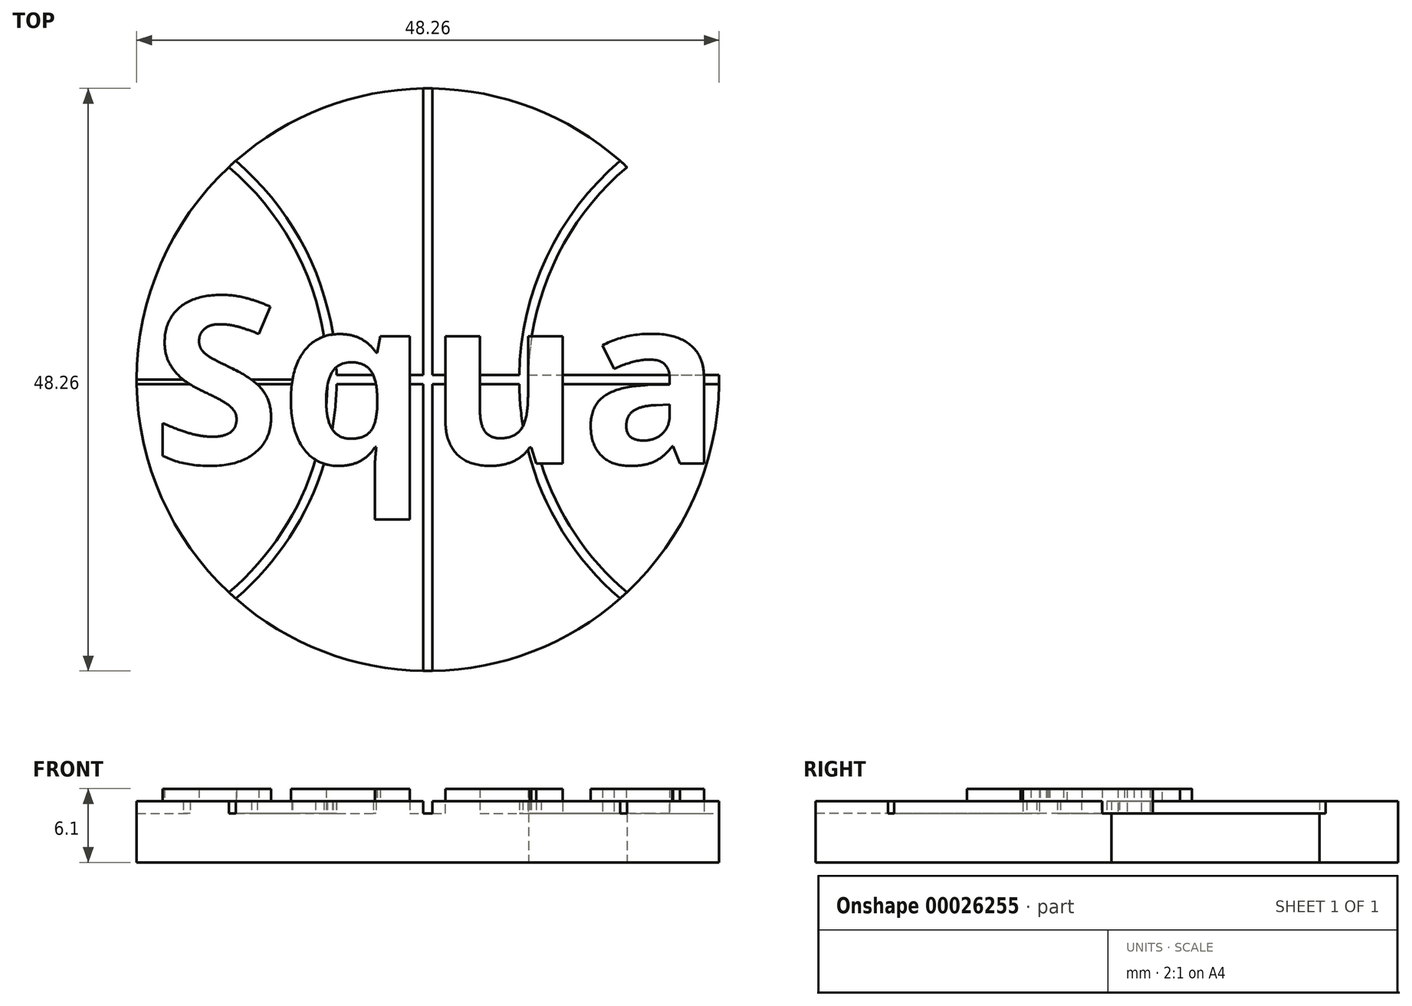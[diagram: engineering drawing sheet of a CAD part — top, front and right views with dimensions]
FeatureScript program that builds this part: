
annotation { "Feature Type Name" : "Feature", "Feature Type Description" : "" }
export const myFeature = defineFeature(function(context is Context, id is Id, definition is map)
    precondition{}
    {
        {
            var Q0;
            Q0=qCreatedBy(makeId("Top.planeOp"),FACE);
            var sketch = newSketch(context, id + "F0", { "sketchPlane" : qUnion([Q0])});
            skCircle(sketch, "E0", {"center": v(0, 0) * mm, "radius": 24.13 * mm});
            skLineSegment(sketch, "E1", {"start": v(-24.13, 0) * mm, "end": v(24.13, 0) * mm});
            skLineSegment(sketch, "E2", {"start": v(0, 24.13) * mm, "end": v(0, -24.13) * mm});
            skArc(sketch, "E3", {"start": v(-16.21, -17.87) * mm, "mid": v(-7.95, 0) * mm, "end": v(-16.21, 17.87) * mm});
            skArc(sketch, "E4.MirrorCS", {"start": v(16.21, -17.87) * mm, "mid": v(7.95, 0) * mm, "end": v(16.21, 17.87) * mm});
            skArc(sketch, "E5.0.startCap", {"start": v(-15.97, -18.16) * mm, "mid": v(-16.5, -18.12) * mm, "end": v(-16.46, -17.58) * mm});
            skArc(sketch, "E5.0.endCap", {"start": v(-16.46, 17.58) * mm, "mid": v(-16.5, 18.12) * mm, "end": v(-15.97, 18.16) * mm});
            skArc(sketch, "E5.0.left", {"start": v(-16.46, -17.58) * mm, "mid": v(-8.33, 0) * mm, "end": v(-16.46, 17.58) * mm});
            skArc(sketch, "E5.0.right", {"start": v(-15.97, -18.16) * mm, "mid": v(-7.56, 0) * mm, "end": v(-15.97, 18.16) * mm});
            skArc(sketch, "E6.0.startCap", {"start": v(-0.38, 24.13) * mm, "mid": v(0, 24.51) * mm, "end": v(0.38, 24.13) * mm});
            skArc(sketch, "E6.0.endCap", {"start": v(0.38, -24.13) * mm, "mid": v(0, -24.51) * mm, "end": v(-0.38, -24.13) * mm});
            skLineSegment(sketch, "E6.0.left", {"start": v(0.38, 24.13) * mm, "end": v(0.38, -24.13) * mm});
            skLineSegment(sketch, "E6.0.right", {"start": v(-0.38, 24.13) * mm, "end": v(-0.38, -24.13) * mm});
            skArc(sketch, "E6.1.startCap", {"start": v(-24.13, -0.38) * mm, "mid": v(-24.51, 0) * mm, "end": v(-24.13, 0.38) * mm});
            skArc(sketch, "E6.1.endCap", {"start": v(24.13, 0.38) * mm, "mid": v(24.51, 0) * mm, "end": v(24.13, -0.38) * mm});
            skLineSegment(sketch, "E6.1.left", {"start": v(-24.13, 0.38) * mm, "end": v(24.13, 0.38) * mm});
            skLineSegment(sketch, "E6.1.right", {"start": v(-24.13, -0.38) * mm, "end": v(24.13, -0.38) * mm});
            skArc(sketch, "E7.0.startCap", {"start": v(16.46, -17.58) * mm, "mid": v(16.5, -18.12) * mm, "end": v(15.97, -18.16) * mm});
            skArc(sketch, "E7.0.endCap", {"start": v(15.97, 18.16) * mm, "mid": v(16.5, 18.12) * mm, "end": v(16.46, 17.58) * mm});
            skArc(sketch, "E7.0.left", {"start": v(15.97, -18.16) * mm, "mid": v(7.56, 0) * mm, "end": v(15.97, 18.16) * mm});
            skArc(sketch, "E7.0.right", {"start": v(16.46, -17.58) * mm, "mid": v(8.33, 0) * mm, "end": v(16.46, 17.58) * mm});
            skSolve(sketch);
        }
        {
            var Q0;
            {var subQ3=sQuery(id+"F0.wireOp",EDGE,"E0");var subQ5=sQuery(id+"F0.wireOp",EDGE,"E5.0.endCap");var subQ7=makeQuery(id+"F0.imprint","INTERSECT",VERTEX,{"derivedFrom":[subQ3,subQ5]});Q0=makeQuery(id+"F0.imprint","IMPRINT",FACE,{"disambiguationData":[TD([[makeQuery(id+"F0.imprint","IMPRINT",EDGE,{"disambiguationData":[TD([[subQ7,-1.0]])],"derivedFrom":subQ3}),1.0]])]});}
            var Q1;
            {var subQ0=sQuery(id+"F0.wireOp",EDGE,"E6.1.right");var subQ3=sQuery(id+"F0.wireOp",EDGE,"E0");var subQ4=makeQuery(id+"F0.imprint","INTERSECT",VERTEX,{"disambiguationData":[OD(0.0)],"derivedFrom":[subQ3,subQ0]});Q1=makeQuery(id+"F0.imprint","IMPRINT",FACE,{"disambiguationData":[TD([[makeQuery(id+"F0.imprint","IMPRINT",EDGE,{"disambiguationData":[TD([[subQ4,-1.0]])],"derivedFrom":subQ3}),1.0]])]});}
            var Q2;
            {var subQ1=sQuery(id+"F0.wireOp",EDGE,"E6.0.right");var subQ5=sQuery(id+"F0.wireOp",EDGE,"E0");var subQ6=makeQuery(id+"F0.imprint","INTERSECT",VERTEX,{"disambiguationData":[OD(0.0)],"derivedFrom":[subQ5,subQ1]});Q2=makeQuery(id+"F0.imprint","IMPRINT",FACE,{"disambiguationData":[TD([[makeQuery(id+"F0.imprint","IMPRINT",EDGE,{"disambiguationData":[TD([[subQ6,-1.0]])],"derivedFrom":subQ5}),1.0]])]});}
            var Q3;
            {var subQ3=sQuery(id+"F0.wireOp",EDGE,"E5.0.right");var subQ5=sQuery(id+"F0.wireOp",EDGE,"E0");var subQ7=makeQuery(id+"F0.imprint","INTERSECT",VERTEX,{"disambiguationData":[OD(1.0)],"derivedFrom":[subQ5,subQ3]});Q3=makeQuery(id+"F0.imprint","IMPRINT",FACE,{"disambiguationData":[TD([[makeQuery(id+"F0.imprint","IMPRINT",EDGE,{"disambiguationData":[TD([[subQ7,-1.0]])],"derivedFrom":subQ5}),1.0]])]});}
            var Q4;
            {var subQ0=sQuery(id+"F0.wireOp",EDGE,"E7.0.left");var subQ3=sQuery(id+"F0.wireOp",EDGE,"E0");var subQ4=makeQuery(id+"F0.imprint","INTERSECT",VERTEX,{"disambiguationData":[OD(0.0)],"derivedFrom":[subQ3,subQ0]});Q4=makeQuery(id+"F0.imprint","IMPRINT",FACE,{"disambiguationData":[TD([[makeQuery(id+"F0.imprint","IMPRINT",EDGE,{"disambiguationData":[TD([[subQ4,-1.0]])],"derivedFrom":subQ3}),1.0]])]});}
            var Q5;
            {var subQ3=sQuery(id+"F0.wireOp",EDGE,"E0");var subQ5=sQuery(id+"F0.wireOp",EDGE,"E6.0.left");var subQ7=makeQuery(id+"F0.imprint","INTERSECT",VERTEX,{"disambiguationData":[OD(1.0)],"derivedFrom":[subQ3,subQ5]});Q5=makeQuery(id+"F0.imprint","IMPRINT",FACE,{"disambiguationData":[TD([[makeQuery(id+"F0.imprint","IMPRINT",EDGE,{"disambiguationData":[TD([[subQ7,-1.0]])],"derivedFrom":subQ3}),1.0]])]});}
            var Q6;
            {var subQ1=sQuery(id+"F0.wireOp",EDGE,"E6.1.left");var subQ5=sQuery(id+"F0.wireOp",EDGE,"E0");var subQ7=makeQuery(id+"F0.imprint","INTERSECT",VERTEX,{"disambiguationData":[OD(0.0)],"derivedFrom":[subQ5,subQ1]});Q6=makeQuery(id+"F0.imprint","IMPRINT",FACE,{"disambiguationData":[TD([[makeQuery(id+"F0.imprint","IMPRINT",EDGE,{"disambiguationData":[TD([[subQ7,-1.0]])],"derivedFrom":subQ5}),1.0]])]});}
            var Q7;
            {var subQ3=sQuery(id+"F0.wireOp",EDGE,"E7.0.startCap");var subQ5=sQuery(id+"F0.wireOp",EDGE,"E0");var subQ6=makeQuery(id+"F0.imprint","INTERSECT",VERTEX,{"derivedFrom":[subQ5,subQ3]});Q7=makeQuery(id+"F0.imprint","IMPRINT",FACE,{"disambiguationData":[TD([[makeQuery(id+"F0.imprint","IMPRINT",EDGE,{"disambiguationData":[TD([[subQ6,-1.0]])],"derivedFrom":subQ5}),1.0]])]});}
            extrude(context, id + "F1", {"entities" : qUnion([Q0, Q1, Q2, Q3, Q4, Q5, Q6, Q7]), "depth" : 5.08 * mm});
        }
        {
            var Q0;
            {var subQ3=sQuery(id+"F0.wireOp",EDGE,"E3");var subQ7=sQuery(id+"F0.wireOp",EDGE,"E0");var subQ9=makeQuery(id+"F0.imprint","INTERSECT",VERTEX,{"disambiguationData":[OD(1.0)],"derivedFrom":[subQ7,subQ3]});Q0=makeQuery(id+"F0.imprint","IMPRINT",FACE,{"disambiguationData":[TD([[makeQuery(id+"F0.imprint","IMPRINT",EDGE,{"disambiguationData":[TD([[subQ9,-1.0]])],"derivedFrom":subQ7}),1.0]])]});}
            var Q1;
            {var subQ3=sQuery(id+"F0.wireOp",EDGE,"E0");var subQ5=sQuery(id+"F0.wireOp",EDGE,"E1");var subQ7=makeQuery(id+"F0.imprint","INTERSECT",VERTEX,{"disambiguationData":[OD(0.0)],"derivedFrom":[subQ3,subQ5]});Q1=makeQuery(id+"F0.imprint","IMPRINT",FACE,{"disambiguationData":[TD([[makeQuery(id+"F0.imprint","IMPRINT",EDGE,{"disambiguationData":[TD([[subQ7,1.0]])],"derivedFrom":subQ3}),1.0]])]});}
            var Q2;
            {var subQ3=sQuery(id+"F0.wireOp",EDGE,"E0");var subQ5=sQuery(id+"F0.wireOp",EDGE,"E1");var subQ7=makeQuery(id+"F0.imprint","INTERSECT",VERTEX,{"disambiguationData":[OD(0.0)],"derivedFrom":[subQ3,subQ5]});Q2=makeQuery(id+"F0.imprint","IMPRINT",FACE,{"disambiguationData":[TD([[makeQuery(id+"F0.imprint","IMPRINT",EDGE,{"disambiguationData":[TD([[subQ7,-1.0]])],"derivedFrom":subQ3}),1.0]])]});}
            var Q3;
            {var subQ1=sQuery(id+"F0.wireOp",EDGE,"E5.0.left");var subQ5=sQuery(id+"F0.wireOp",EDGE,"E1");var subQ6=makeQuery(id+"F0.imprint","INTERSECT",VERTEX,{"derivedFrom":[subQ5,subQ1]});Q3=makeQuery(id+"F0.imprint","IMPRINT",FACE,{"disambiguationData":[TD([[makeQuery(id+"F0.imprint","IMPRINT",EDGE,{"disambiguationData":[TD([[subQ6,-1.0]])],"derivedFrom":subQ5}),1.0]])]});}
            var Q4;
            {var subQ3=sQuery(id+"F0.wireOp",EDGE,"E3");var subQ5=sQuery(id+"F0.wireOp",EDGE,"E1");var subQ7=makeQuery(id+"F0.imprint","INTERSECT",VERTEX,{"derivedFrom":[subQ5,subQ3]});Q4=makeQuery(id+"F0.imprint","IMPRINT",FACE,{"disambiguationData":[TD([[makeQuery(id+"F0.imprint","IMPRINT",EDGE,{"disambiguationData":[TD([[subQ7,-1.0]])],"derivedFrom":subQ5}),1.0]])]});}
            var Q5;
            {var subQ3=sQuery(id+"F0.wireOp",EDGE,"E3");var subQ5=sQuery(id+"F0.wireOp",EDGE,"E1");var subQ7=makeQuery(id+"F0.imprint","INTERSECT",VERTEX,{"derivedFrom":[subQ5,subQ3]});Q5=makeQuery(id+"F0.imprint","IMPRINT",FACE,{"disambiguationData":[TD([[makeQuery(id+"F0.imprint","IMPRINT",EDGE,{"disambiguationData":[TD([[subQ7,-1.0]])],"derivedFrom":subQ5}),-1.0]])]});}
            var Q6;
            {var subQ1=sQuery(id+"F0.wireOp",EDGE,"E5.0.left");var subQ5=sQuery(id+"F0.wireOp",EDGE,"E1");var subQ6=makeQuery(id+"F0.imprint","INTERSECT",VERTEX,{"derivedFrom":[subQ5,subQ1]});Q6=makeQuery(id+"F0.imprint","IMPRINT",FACE,{"disambiguationData":[TD([[makeQuery(id+"F0.imprint","IMPRINT",EDGE,{"disambiguationData":[TD([[subQ6,-1.0]])],"derivedFrom":subQ5}),-1.0]])]});}
            var Q7;
            {var subQ3=sQuery(id+"F0.wireOp",EDGE,"E3");var subQ5=sQuery(id+"F0.wireOp",EDGE,"E0");var subQ7=makeQuery(id+"F0.imprint","INTERSECT",VERTEX,{"disambiguationData":[OD(1.0)],"derivedFrom":[subQ5,subQ3]});Q7=makeQuery(id+"F0.imprint","IMPRINT",FACE,{"disambiguationData":[TD([[makeQuery(id+"F0.imprint","IMPRINT",EDGE,{"disambiguationData":[TD([[subQ7,1.0]])],"derivedFrom":subQ5}),1.0]])]});}
            var Q8;
            {var subQ3=sQuery(id+"F0.wireOp",EDGE,"E3");var subQ5=sQuery(id+"F0.wireOp",EDGE,"E0");var subQ7=makeQuery(id+"F0.imprint","INTERSECT",VERTEX,{"disambiguationData":[OD(0.0)],"derivedFrom":[subQ5,subQ3]});Q8=makeQuery(id+"F0.imprint","IMPRINT",FACE,{"disambiguationData":[TD([[makeQuery(id+"F0.imprint","IMPRINT",EDGE,{"disambiguationData":[TD([[subQ7,-1.0]])],"derivedFrom":subQ5}),1.0]])]});}
            var Q9;
            {var subQ3=sQuery(id+"F0.wireOp",EDGE,"E3");var subQ7=sQuery(id+"F0.wireOp",EDGE,"E0");var subQ9=makeQuery(id+"F0.imprint","INTERSECT",VERTEX,{"disambiguationData":[OD(0.0)],"derivedFrom":[subQ7,subQ3]});Q9=makeQuery(id+"F0.imprint","IMPRINT",FACE,{"disambiguationData":[TD([[makeQuery(id+"F0.imprint","IMPRINT",EDGE,{"disambiguationData":[TD([[subQ9,1.0]])],"derivedFrom":subQ7}),1.0]])]});}
            var Q10;
            {var subQ3=sQuery(id+"F0.wireOp",EDGE,"E5.0.right");var subQ5=sQuery(id+"F0.wireOp",EDGE,"E1");var subQ7=makeQuery(id+"F0.imprint","INTERSECT",VERTEX,{"derivedFrom":[subQ5,subQ3]});Q10=makeQuery(id+"F0.imprint","IMPRINT",FACE,{"disambiguationData":[TD([[makeQuery(id+"F0.imprint","IMPRINT",EDGE,{"disambiguationData":[TD([[subQ7,-1.0]])],"derivedFrom":subQ5}),1.0]])]});}
            var Q11;
            {var subQ3=sQuery(id+"F0.wireOp",EDGE,"E5.0.right");var subQ5=sQuery(id+"F0.wireOp",EDGE,"E1");var subQ7=makeQuery(id+"F0.imprint","INTERSECT",VERTEX,{"derivedFrom":[subQ5,subQ3]});Q11=makeQuery(id+"F0.imprint","IMPRINT",FACE,{"disambiguationData":[TD([[makeQuery(id+"F0.imprint","IMPRINT",EDGE,{"disambiguationData":[TD([[subQ7,-1.0]])],"derivedFrom":subQ5}),-1.0]])]});}
            var Q12;
            {var subQ1=sQuery(id+"F0.wireOp",EDGE,"E6.0.right");var subQ5=sQuery(id+"F0.wireOp",EDGE,"E1");var subQ6=makeQuery(id+"F0.imprint","INTERSECT",VERTEX,{"derivedFrom":[subQ5,subQ1]});Q12=makeQuery(id+"F0.imprint","IMPRINT",FACE,{"disambiguationData":[TD([[makeQuery(id+"F0.imprint","IMPRINT",EDGE,{"disambiguationData":[TD([[subQ6,-1.0]])],"derivedFrom":subQ5}),1.0]])]});}
            var Q13;
            {var subQ3=sQuery(id+"F0.wireOp",EDGE,"E2");var subQ5=sQuery(id+"F0.wireOp",EDGE,"E1");var subQ7=makeQuery(id+"F0.imprint","INTERSECT",VERTEX,{"derivedFrom":[subQ5,subQ3]});Q13=makeQuery(id+"F0.imprint","IMPRINT",FACE,{"disambiguationData":[TD([[makeQuery(id+"F0.imprint","IMPRINT",EDGE,{"disambiguationData":[TD([[subQ7,-1.0]])],"derivedFrom":subQ5}),1.0]])]});}
            var Q14;
            {var subQ3=sQuery(id+"F0.wireOp",EDGE,"E2");var subQ5=sQuery(id+"F0.wireOp",EDGE,"E1");var subQ7=makeQuery(id+"F0.imprint","INTERSECT",VERTEX,{"derivedFrom":[subQ5,subQ3]});Q14=makeQuery(id+"F0.imprint","IMPRINT",FACE,{"disambiguationData":[TD([[makeQuery(id+"F0.imprint","IMPRINT",EDGE,{"disambiguationData":[TD([[subQ7,-1.0]])],"derivedFrom":subQ5}),-1.0]])]});}
            var Q15;
            {var subQ1=sQuery(id+"F0.wireOp",EDGE,"E6.0.right");var subQ5=sQuery(id+"F0.wireOp",EDGE,"E1");var subQ6=makeQuery(id+"F0.imprint","INTERSECT",VERTEX,{"derivedFrom":[subQ5,subQ1]});Q15=makeQuery(id+"F0.imprint","IMPRINT",FACE,{"disambiguationData":[TD([[makeQuery(id+"F0.imprint","IMPRINT",EDGE,{"disambiguationData":[TD([[subQ6,-1.0]])],"derivedFrom":subQ5}),-1.0]])]});}
            var Q16;
            {var subQ3=sQuery(id+"F0.wireOp",EDGE,"E2");var subQ5=sQuery(id+"F0.wireOp",EDGE,"E0");var subQ7=makeQuery(id+"F0.imprint","INTERSECT",VERTEX,{"disambiguationData":[OD(0.0)],"derivedFrom":[subQ5,subQ3]});Q16=makeQuery(id+"F0.imprint","IMPRINT",FACE,{"disambiguationData":[TD([[makeQuery(id+"F0.imprint","IMPRINT",EDGE,{"disambiguationData":[TD([[subQ7,-1.0]])],"derivedFrom":subQ5}),1.0]])]});}
            var Q17;
            {var subQ3=sQuery(id+"F0.wireOp",EDGE,"E2");var subQ5=sQuery(id+"F0.wireOp",EDGE,"E0");var subQ7=makeQuery(id+"F0.imprint","INTERSECT",VERTEX,{"disambiguationData":[OD(0.0)],"derivedFrom":[subQ5,subQ3]});Q17=makeQuery(id+"F0.imprint","IMPRINT",FACE,{"disambiguationData":[TD([[makeQuery(id+"F0.imprint","IMPRINT",EDGE,{"disambiguationData":[TD([[subQ7,1.0]])],"derivedFrom":subQ5}),1.0]])]});}
            var Q18;
            {var subQ3=sQuery(id+"F0.wireOp",EDGE,"E2");var subQ5=sQuery(id+"F0.wireOp",EDGE,"E0");var subQ7=makeQuery(id+"F0.imprint","INTERSECT",VERTEX,{"disambiguationData":[OD(1.0)],"derivedFrom":[subQ5,subQ3]});Q18=makeQuery(id+"F0.imprint","IMPRINT",FACE,{"disambiguationData":[TD([[makeQuery(id+"F0.imprint","IMPRINT",EDGE,{"disambiguationData":[TD([[subQ7,-1.0]])],"derivedFrom":subQ5}),1.0]])]});}
            var Q19;
            {var subQ3=sQuery(id+"F0.wireOp",EDGE,"E2");var subQ5=sQuery(id+"F0.wireOp",EDGE,"E0");var subQ7=makeQuery(id+"F0.imprint","INTERSECT",VERTEX,{"disambiguationData":[OD(1.0)],"derivedFrom":[subQ5,subQ3]});Q19=makeQuery(id+"F0.imprint","IMPRINT",FACE,{"disambiguationData":[TD([[makeQuery(id+"F0.imprint","IMPRINT",EDGE,{"disambiguationData":[TD([[subQ7,1.0]])],"derivedFrom":subQ5}),1.0]])]});}
            var Q20;
            {var subQ3=sQuery(id+"F0.wireOp",EDGE,"E1");var subQ5=sQuery(id+"F0.wireOp",EDGE,"E6.0.left");var subQ7=makeQuery(id+"F0.imprint","INTERSECT",VERTEX,{"derivedFrom":[subQ3,subQ5]});Q20=makeQuery(id+"F0.imprint","IMPRINT",FACE,{"disambiguationData":[TD([[makeQuery(id+"F0.imprint","IMPRINT",EDGE,{"disambiguationData":[TD([[subQ7,-1.0]])],"derivedFrom":subQ3}),1.0]])]});}
            var Q21;
            {var subQ3=sQuery(id+"F0.wireOp",EDGE,"E6.0.left");var subQ5=sQuery(id+"F0.wireOp",EDGE,"E1");var subQ7=makeQuery(id+"F0.imprint","INTERSECT",VERTEX,{"derivedFrom":[subQ5,subQ3]});Q21=makeQuery(id+"F0.imprint","IMPRINT",FACE,{"disambiguationData":[TD([[makeQuery(id+"F0.imprint","IMPRINT",EDGE,{"disambiguationData":[TD([[subQ7,-1.0]])],"derivedFrom":subQ5}),-1.0]])]});}
            var Q22;
            {var subQ3=sQuery(id+"F0.wireOp",EDGE,"E1");var subQ5=sQuery(id+"F0.wireOp",EDGE,"E0");var subQ7=makeQuery(id+"F0.imprint","INTERSECT",VERTEX,{"disambiguationData":[OD(1.0)],"derivedFrom":[subQ5,subQ3]});Q22=makeQuery(id+"F0.imprint","IMPRINT",FACE,{"disambiguationData":[TD([[makeQuery(id+"F0.imprint","IMPRINT",EDGE,{"disambiguationData":[TD([[subQ7,1.0]])],"derivedFrom":subQ5}),1.0]])]});}
            var Q23;
            {var subQ3=sQuery(id+"F0.wireOp",EDGE,"E1");var subQ5=sQuery(id+"F0.wireOp",EDGE,"E0");var subQ7=makeQuery(id+"F0.imprint","INTERSECT",VERTEX,{"disambiguationData":[OD(1.0)],"derivedFrom":[subQ5,subQ3]});Q23=makeQuery(id+"F0.imprint","IMPRINT",FACE,{"disambiguationData":[TD([[makeQuery(id+"F0.imprint","IMPRINT",EDGE,{"disambiguationData":[TD([[subQ7,-1.0]])],"derivedFrom":subQ5}),1.0]])]});}
            var Q24;
            {var subQ3=sQuery(id+"F0.wireOp",EDGE,"E1");var subQ5=sQuery(id+"F0.wireOp",EDGE,"E4.MirrorCS");var subQ7=makeQuery(id+"F0.imprint","INTERSECT",VERTEX,{"derivedFrom":[subQ3,subQ5]});Q24=makeQuery(id+"F0.imprint","IMPRINT",FACE,{"disambiguationData":[TD([[makeQuery(id+"F0.imprint","IMPRINT",EDGE,{"disambiguationData":[TD([[subQ7,-1.0]])],"derivedFrom":subQ3}),1.0]])]});}
            var Q25;
            {var subQ5=sQuery(id+"F0.wireOp",EDGE,"E0");var subQ7=sQuery(id+"F0.wireOp",EDGE,"E4.MirrorCS");var subQ9=makeQuery(id+"F0.imprint","INTERSECT",VERTEX,{"disambiguationData":[OD(1.0)],"derivedFrom":[subQ5,subQ7]});Q25=makeQuery(id+"F0.imprint","IMPRINT",FACE,{"disambiguationData":[TD([[makeQuery(id+"F0.imprint","IMPRINT",EDGE,{"disambiguationData":[TD([[subQ9,1.0]])],"derivedFrom":subQ5}),1.0]])]});}
            var Q26;
            {var subQ3=sQuery(id+"F0.wireOp",EDGE,"E0");var subQ5=sQuery(id+"F0.wireOp",EDGE,"E4.MirrorCS");var subQ7=makeQuery(id+"F0.imprint","INTERSECT",VERTEX,{"disambiguationData":[OD(1.0)],"derivedFrom":[subQ3,subQ5]});Q26=makeQuery(id+"F0.imprint","IMPRINT",FACE,{"disambiguationData":[TD([[makeQuery(id+"F0.imprint","IMPRINT",EDGE,{"disambiguationData":[TD([[subQ7,-1.0]])],"derivedFrom":subQ3}),1.0]])]});}
            var Q27;
            {var subQ0=sQuery(id+"F0.wireOp",EDGE,"E7.0.left");var subQ3=sQuery(id+"F0.wireOp",EDGE,"E1");var subQ4=makeQuery(id+"F0.imprint","INTERSECT",VERTEX,{"derivedFrom":[subQ3,subQ0]});Q27=makeQuery(id+"F0.imprint","IMPRINT",FACE,{"disambiguationData":[TD([[makeQuery(id+"F0.imprint","IMPRINT",EDGE,{"disambiguationData":[TD([[subQ4,-1.0]])],"derivedFrom":subQ3}),1.0]])]});}
            var Q28;
            {var subQ3=sQuery(id+"F0.wireOp",EDGE,"E0");var subQ5=sQuery(id+"F0.wireOp",EDGE,"E4.MirrorCS");var subQ7=makeQuery(id+"F0.imprint","INTERSECT",VERTEX,{"disambiguationData":[OD(0.0)],"derivedFrom":[subQ3,subQ5]});Q28=makeQuery(id+"F0.imprint","IMPRINT",FACE,{"disambiguationData":[TD([[makeQuery(id+"F0.imprint","IMPRINT",EDGE,{"disambiguationData":[TD([[subQ7,1.0]])],"derivedFrom":subQ3}),1.0]])]});}
            var Q29;
            {var subQ5=sQuery(id+"F0.wireOp",EDGE,"E0");var subQ7=sQuery(id+"F0.wireOp",EDGE,"E4.MirrorCS");var subQ9=makeQuery(id+"F0.imprint","INTERSECT",VERTEX,{"disambiguationData":[OD(0.0)],"derivedFrom":[subQ5,subQ7]});Q29=makeQuery(id+"F0.imprint","IMPRINT",FACE,{"disambiguationData":[TD([[makeQuery(id+"F0.imprint","IMPRINT",EDGE,{"disambiguationData":[TD([[subQ9,-1.0]])],"derivedFrom":subQ5}),1.0]])]});}
            var Q30;
            {var subQ0=sQuery(id+"F0.wireOp",EDGE,"E7.0.left");var subQ3=sQuery(id+"F0.wireOp",EDGE,"E1");var subQ4=makeQuery(id+"F0.imprint","INTERSECT",VERTEX,{"derivedFrom":[subQ3,subQ0]});Q30=makeQuery(id+"F0.imprint","IMPRINT",FACE,{"disambiguationData":[TD([[makeQuery(id+"F0.imprint","IMPRINT",EDGE,{"disambiguationData":[TD([[subQ4,-1.0]])],"derivedFrom":subQ3}),-1.0]])]});}
            var Q31;
            {var subQ3=sQuery(id+"F0.wireOp",EDGE,"E1");var subQ5=sQuery(id+"F0.wireOp",EDGE,"E4.MirrorCS");var subQ7=makeQuery(id+"F0.imprint","INTERSECT",VERTEX,{"derivedFrom":[subQ3,subQ5]});Q31=makeQuery(id+"F0.imprint","IMPRINT",FACE,{"disambiguationData":[TD([[makeQuery(id+"F0.imprint","IMPRINT",EDGE,{"disambiguationData":[TD([[subQ7,-1.0]])],"derivedFrom":subQ3}),-1.0]])]});}
            extrude(context, id + "F2", {"entities" : qUnion([Q0, Q1, Q2, Q3, Q4, Q5, Q6, Q7, Q8, Q9, Q10, Q11, Q12, Q13, Q14, Q15, Q16, Q17, Q18, Q19, Q20, Q21, Q22, Q23, Q24, Q25, Q26, Q27, Q28, Q29, Q30, Q31]), "depth" : 4.06 * mm});
        }
        {
            var Q0;
            Q0=makeQuery(id+"F1.opExtrude","CAP_FACE",FACE,{"disambiguationData":[OSD([sQuery(id+"F0.wireOp",EDGE,"E0"),sQuery(id+"F0.wireOp",EDGE,"E5.0.right"),sQuery(id+"F0.wireOp",EDGE,"E6.0.right"),sQuery(id+"F0.wireOp",EDGE,"E6.1.left")])],"isStart":false});
            var sketch = newSketch(context, id + "F3", { "sketchPlane" : qUnion([Q0])});
            skText(sketch, "E8", { "text": "Squa", "fontName": "OpenSans-Bold.ttf"});
            const initialGuessF3  = {"E8": [-0.02286, -0.00695, 1, 0, 0.0139]};
            skSetInitialGuess(sketch, initialGuessF3);
            skSolve(sketch);
        }
        {
            var Q0;
            Q0 = qSketchRegion(id + "F3", true);
            extrude(context, id + "F4", {"entities" : qUnion([Q0]), "operationType" : NewBodyOperationType.ADD, "depth" : 1.02 * mm, "hasSecondDirection" : true, "secondDirectionOppositeDirection" : true, "secondDirectionDepth" : 1.02 * mm});
        }
    });
